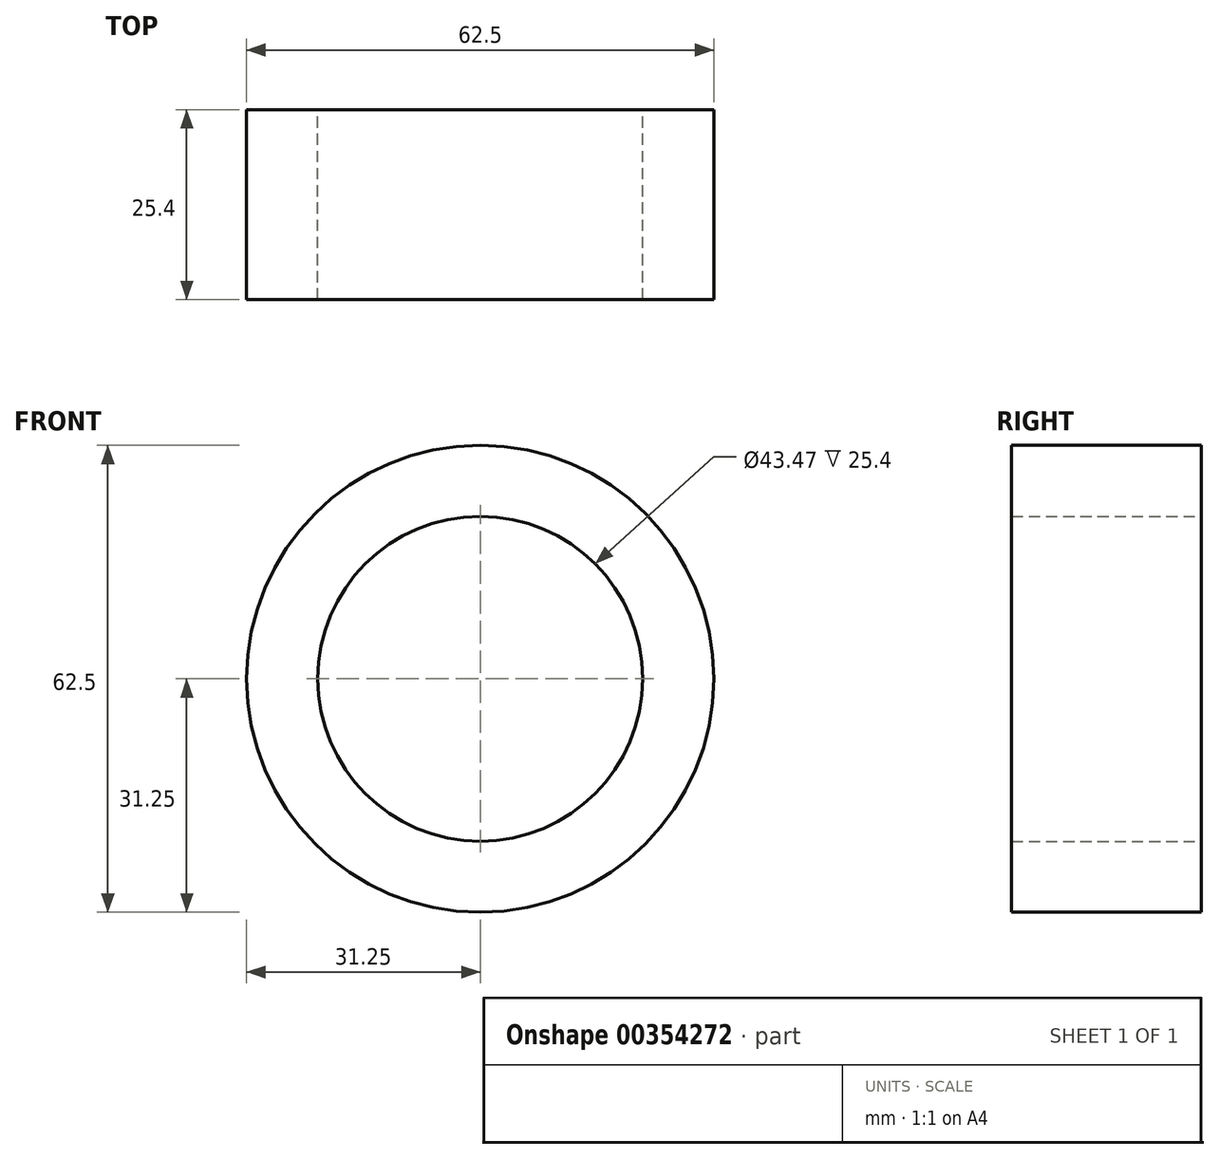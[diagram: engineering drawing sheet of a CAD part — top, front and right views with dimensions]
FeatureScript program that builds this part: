
annotation { "Feature Type Name" : "Feature", "Feature Type Description" : "" }
export const myFeature = defineFeature(function(context is Context, id is Id, definition is map)
    precondition{}
    {
        {
            var Q0;
            Q0=qCreatedBy(makeId("Front.planeOp"),FACE);
            var sketch = newSketch(context, id + "F0", { "sketchPlane" : qUnion([Q0])});
            skCircle(sketch, "E0", {"center": v(0, 0) * mm, "radius": 31.25 * mm});
            skCircle(sketch, "E1", {"center": v(0, 0) * mm, "radius": 21.74 * mm});
            skSolve(sketch);
        }
        {
            var Q0;
            Q0 = qSketchRegion(id + "F0", true);
            extrude(context, id + "F1", {"entities" : qUnion([Q0]), "depth" : 25.4 * mm});
        }
    });
